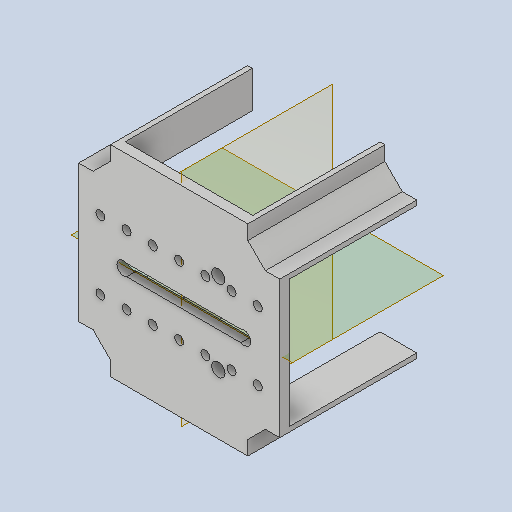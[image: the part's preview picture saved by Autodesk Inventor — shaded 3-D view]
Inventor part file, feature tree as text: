
AUTODESK INVENTOR PART (.ipt)
format: ipt  version: 2023 (Build 270158000, 158)  size: 287,744 bytes
history: native  units: mm
features: plane x9, sketch x6, extrude x5, other x5, projected_geometry x2, reference x2, hole x1, pattern_linear x1
ambient origin geometry x8: Origin, YZ Plane, XZ Plane, XY Plane, X Axis, Y Axis, Z Axis, Center Point
bodies: Body1 (feature_tree)
feature tree (31):
  plane  "Work Plane1"
  plane  "Work Plane2"
  plane  "Work Plane4"
  extrude  "Extrusion1"  Depth=24.9mm
  hole  "Hole1"  [1 undecoded]
  extrude  "IM_offset"  Depth=2.43mm TaperAngle=0.0deg
  extrude  "Extrusion6"  Depth=0.2mm
  plane  "Work Plane3"
  sketch  "Sketch9"  dims[d26=1.0mm d27=0.0mm d28=2.9mm]
  plane  "Work Plane5"
  extrude  "Extrusion9"  Depth=2.9mm
  plane  "Work Plane6"
  plane  "Work Plane7"
  plane  "Arbeitsebene8"
  plane  "Arbeitsebene9"
  extrude  "Extrusion12"  Depth=1.2mm
  pattern_linear  "Rechteckige Anordnung1"  Spacing1=31.5mm  [1 undecoded]
  sketch  "Sketch1"  dims[d0=45.0deg d2=24.9mm]
  sketch  "Sketch5"  dims[d3=3.14mm d4=26.9mm]
  sketch  "Skizze6"  dims[d5=20.0mm d6=2.43mm d7=0.0mm]
  projected_geometry  "Projizierte Kontur2"
  sketch  "Sketch7"  dims[d18=3.3mm d19=6.0mm d20=4.0mm d21=2.0mm d22=90.0deg d23=12.0mm d24=20.594885mm d25=0.2mm]
  sketch  "Skizze13"  dims[d29=10.0mm d30=0.0mm d44=1.2mm d49=31.5mm d50=0.0mm d55=2.2mm d56=2.2mm d57=8.5mm d58=8.5mm d59=31.5mm d60=0.0mm d61=70.0mm d63=6.5mm d64=1.2mm d65=40.0mm d67=360.0deg]
  projected_geometry  "Projizierte Kontur6"
  reference  "Referenz2"
  reference  "Referenz3"
  other  "Assembly_Cube_Z-Stage_NEMA11_china_v3.iam"
  other  "Assembly_Cube_empty_IM_v3:2"
  other  "10_Cube_1x1_IM:2"
  other  "Assembly_Cube_empty_IM_v3:1"
  other  "10_Cube_1x1_IM:1"
note: 2 required parameter values undecoded (feature->parameter linkage not recoverable at this tier; creation-order binding heuristic only, values carry confidence <= 0.55)
